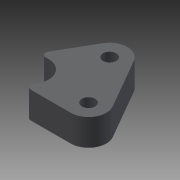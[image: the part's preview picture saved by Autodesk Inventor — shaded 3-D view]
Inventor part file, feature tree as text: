
AUTODESK INVENTOR PART (.ipt)
format: ipt  version: 2013 (Build 170138000, 138)  size: 105,984 bytes
history: native  units: mm
features: extrude x1, sketch x1
ambient origin geometry x8: Origin, YZ Plane, XZ Plane, XY Plane, X Axis, Y Axis, Z Axis, Center Point
bodies: Solid1 (feature_tree)
feature tree (2):
  extrude  "Extrusion1"  Depth=8.0mm
  sketch  "Sketch1"  dims[d0=3.0mm d1=3.0mm d3=13.0mm d4=13.0mm d24=60.0deg d25=8.0mm d26=8.0mm d27=8.0mm d28=6.0mm d29=0.0mm d30=1.0mm]
